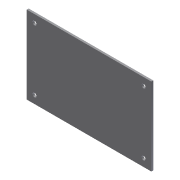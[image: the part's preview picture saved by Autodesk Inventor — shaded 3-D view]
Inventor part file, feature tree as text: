
AUTODESK INVENTOR PART (.ipt)
format: ipt  version: 2012 (Build 160160000, 160)  size: 80,896 bytes
history: native  units: in
note: dims shown in document units (in); Inventor stores cm internally (conversion verified against a paired STEP export)
features: extrude x1, sketch x1
ambient origin geometry x8: Origin, YZ Plane, XZ Plane, XY Plane, X Axis, Y Axis, Z Axis, Center Point
feature tree (2):
  extrude  "Extrusion2"  Depth=8.0in
  sketch  "Sketch1"  dims[d0=5.0in d1=8.0in d4=0.5in d5=0.5in d6=0.5in d7=0.5in d8=0.5in d9=0.5in d10=0.5in d11=0.25in d12=0.25in d13=0.5in d14=0.25in d15=0.25in d16=0.125in d17=0.0in]
